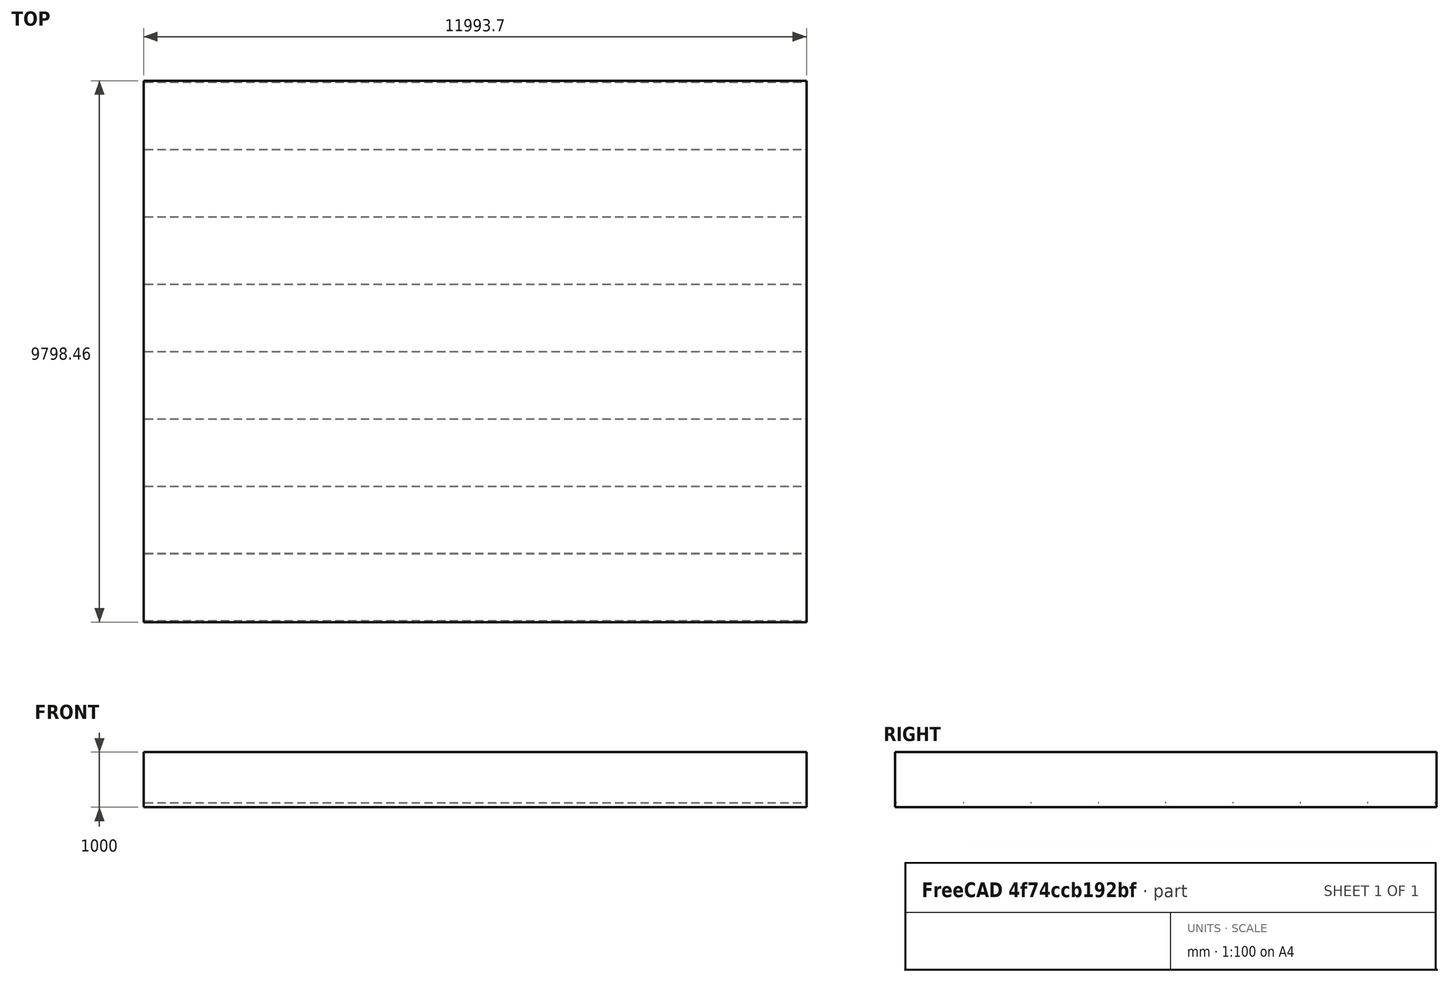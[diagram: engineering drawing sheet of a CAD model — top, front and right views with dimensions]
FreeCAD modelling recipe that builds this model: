
FCSTD DOCUMENT  (FreeCAD 0.21R33771 (Git))
Label: slab with reinforcement
License: All rights reserved
objects: Part::FeaturePython×2, Part::Part2DObjectPython×1, Sketcher::SketchObject×1
note: 4 computed .brp shape members not serialized (recipe doc carries the construction recipe); baked Part::Feature solids carry a one-line shape summary decoded from their .brp

FEATURE [Part::Part2DObjectPython] Rectangle  # Draft 2D object (typed FeaturePython)
  Area = 1.1752e+08
  ChamferSize = 0
  Columns = 1
  FilletRadius = 0
  Height = 9798.45
  Length = 11993.7
  MakeFace = true
  Placement = pos=(-20016.6,180.931,0) rot=(0,0,1;0rad)
  Rows = 1
FEATURE [Part::FeaturePython] Structure  # Arch/BIM 13 (typed FeaturePython)
  Base = -> Rectangle
  BaseMirror = false
  BaseOffsetX = 0
  BaseOffsetY = 0
  BasePerpendicularToTool = false
  BaseRotation = 0
  ComputedLength = 1000
  FaceMaker = 0
  Height = 1000
  HorizontalArea = 1.1752e+08
  IfcData = attributes={"GlobalId": {"name": "GlobalId", "type": "IfcGloballyUniqueId", "is_enum": false, "enum_values": []}, "Description": {"... (+484 chars omitted),+1 more (map truncated)
  IfcType = 13
  Length = 0
  MoveBase = false
  MoveWithHost = false
  Nodes = (2) [(-14019.8,5080.16,0),(-14019.8,5080.16,1000)]
  NodesOffset = 0
  Normal = (0,0,0)
  PerimeterLength = 43584.4
  PredefinedType = 0
  ToolOffsetFirst = 0
  ToolOffsetLast = 0
  VerticalArea = 4.35844e+07
  Width = 100
FEATURE [Sketcher::SketchObject] Sketch
  FullyConstrained = false
  MapMode = 5
  Placement = pos=(-1.11e-14,180.931,0) rot=(1,0,0;1.5708rad)
  Support = -> [Structure]
  sketch-geometry (1):
    g0: LineSegment StartX=-19996.6 StartY=84 StartZ=0 EndX=-8042.89 EndY=84 EndZ=0
FEATURE [Part::FeaturePython] Rebar  label="StraightRebar"  # Arch/BIM 110 (typed FeaturePython)
  Amount = 9
  AmountCheck = true
  Base = -> Sketch
  Cover = 80
  CoverAlong = Bottom Side
  Diameter = 8
  Direction = (0,0,0)
  Distance = 0
  FrontCover = 20
  HorizontalArea = 0
  Host = -> Structure
  IfcType = 110
  LeftBottomCover = 20
  Length = 11953.7
  Mark = StraightRebar
  MoveBase = false
  MoveWithHost = false
  OffsetEnd = 24
  OffsetStart = 24
  Orientation = Horizontal
  PerimeterLength = 0
  PlacementList = 9 placements: arithmetic series from (-1.46958e-15,24,-5.32907e-15) step (-7.46304e-14,1218.81,-2.70629e-13) to (-5.98513e-13,9774.45,-2.17036e-12)
  RebarShape = 0
  RightTopCover = 20
  Rounding = 0
  Spacing = 1218.81
  TotalLength = 107584
  TrueSpacing = 9
  VerticalArea = 0
